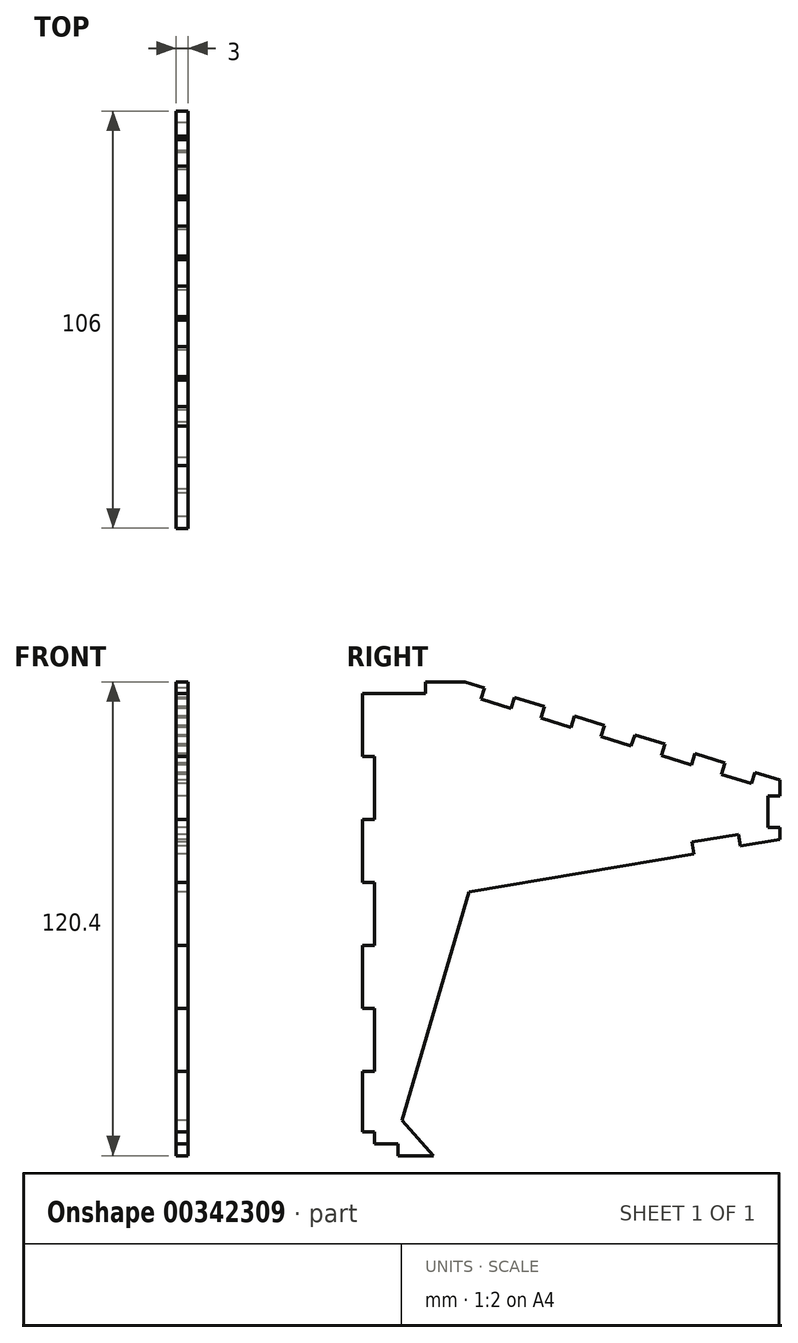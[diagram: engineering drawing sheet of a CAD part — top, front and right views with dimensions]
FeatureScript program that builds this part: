
annotation { "Feature Type Name" : "Feature", "Feature Type Description" : "" }
export const myFeature = defineFeature(function(context is Context, id is Id, definition is map)
    precondition{}
    {
        {
            var Q0;
            Q0=qCreatedBy(makeId("Right.planeOp"),FACE);
            var sketch = newSketch(context, id + "F0", { "sketchPlane" : qUnion([Q0])});
            skLineSegment(sketch, "E0.top", {"start": v(-28.67, -48.45) * mm, "end": v(-19.67, -48.45) * mm});
            skLineSegment(sketch, "E1", {"start": v(-37.67, 71.95) * mm, "end": v(-21.67, 71.95) * mm, "construction": true});
            skLineSegment(sketch, "E2", {"start": v(-21.67, 71.95) * mm, "end": v(-11.67, 71.95) * mm});
            skLineSegment(sketch, "E3", {"start": v(-21.67, 71.95) * mm, "end": v(-21.67, 68.95) * mm});
            skLineSegment(sketch, "E4", {"start": v(-21.67, 68.95) * mm, "end": v(-37.67, 68.95) * mm});
            skLineSegment(sketch, "E5", {"start": v(-37.67, 68.95) * mm, "end": v(-37.67, 52.95) * mm});
            skLineSegment(sketch, "E6", {"start": v(-37.67, 52.95) * mm, "end": v(-34.67, 52.95) * mm});
            skLineSegment(sketch, "E7", {"start": v(-34.67, 52.95) * mm, "end": v(-34.67, 36.95) * mm});
            skLineSegment(sketch, "E8", {"start": v(-34.67, 36.95) * mm, "end": v(-37.67, 36.95) * mm});
            skLineSegment(sketch, "E9", {"start": v(-37.67, 36.95) * mm, "end": v(-37.67, 20.95) * mm});
            skLineSegment(sketch, "E10", {"start": v(-37.67, 20.95) * mm, "end": v(-34.67, 20.95) * mm});
            skLineSegment(sketch, "E11", {"start": v(-34.67, 20.95) * mm, "end": v(-34.67, 4.95) * mm});
            skLineSegment(sketch, "E12", {"start": v(-34.67, 4.95) * mm, "end": v(-37.67, 4.95) * mm});
            skLineSegment(sketch, "E13", {"start": v(-37.67, 4.95) * mm, "end": v(-37.67, -11.05) * mm});
            skLineSegment(sketch, "E14", {"start": v(-37.67, -11.05) * mm, "end": v(-34.67, -11.05) * mm});
            skLineSegment(sketch, "E15", {"start": v(-34.67, -11.05) * mm, "end": v(-34.67, -27.05) * mm});
            skLineSegment(sketch, "E16", {"start": v(-34.67, -27.05) * mm, "end": v(-37.67, -27.05) * mm});
            skLineSegment(sketch, "E17", {"start": v(-37.67, -27.05) * mm, "end": v(-37.67, -42.45) * mm});
            skLineSegment(sketch, "E18", {"start": v(-37.67, -42.45) * mm, "end": v(-34.67, -42.45) * mm});
            skLineSegment(sketch, "E19", {"start": v(-34.67, -42.45) * mm, "end": v(-34.67, -45.45) * mm});
            skLineSegment(sketch, "E20", {"start": v(-34.67, -45.45) * mm, "end": v(-28.67, -45.45) * mm});
            skLineSegment(sketch, "E21", {"start": v(-28.67, -45.45) * mm, "end": v(-28.67, -48.45) * mm});
            skLineSegment(sketch, "E22", {"start": v(68.33, 46.95) * mm, "end": v(68.33, 42.95) * mm});
            skLineSegment(sketch, "E23", {"start": v(68.33, 42.95) * mm, "end": v(65.33, 42.95) * mm});
            skLineSegment(sketch, "E24", {"start": v(65.33, 42.95) * mm, "end": v(65.33, 34.95) * mm});
            skLineSegment(sketch, "E25", {"start": v(65.33, 34.95) * mm, "end": v(68.33, 34.95) * mm});
            skLineSegment(sketch, "E26", {"start": v(68.33, 34.95) * mm, "end": v(68.33, 31.95) * mm});
            skLineSegment(sketch, "E27", {"start": v(-19.67, -48.45) * mm, "end": v(-27.67, -39.45) * mm});
            skLineSegment(sketch, "E28", {"start": v(-10.67, 18.55) * mm, "end": v(-27.67, -39.45) * mm});
            skLineSegment(sketch, "E29", {"start": v(46.5, 28.24) * mm, "end": v(46, 31.2) * mm});
            skLineSegment(sketch, "E30", {"start": v(46, 31.2) * mm, "end": v(57.83, 33.2) * mm});
            skLineSegment(sketch, "E31", {"start": v(57.83, 33.2) * mm, "end": v(58.33, 30.25) * mm});
            skLineSegment(sketch, "E32", {"start": v(-10.67, 18.55) * mm, "end": v(46.5, 28.24) * mm});
            skLineSegment(sketch, "E33", {"start": v(58.33, 30.25) * mm, "end": v(68.33, 31.95) * mm});
            skLineSegment(sketch, "E34", {"start": v(46.5, 28.24) * mm, "end": v(58.33, 30.25) * mm, "construction": true});
            skLineSegment(sketch, "E35", {"start": v(68.33, 46.95) * mm, "end": v(68.33, 56.95) * mm, "construction": true});
            skLineSegment(sketch, "E36", {"start": v(-11.67, 81.95) * mm, "end": v(-11.67, 71.95) * mm, "construction": true});
            skLineSegment(sketch, "E37", {"start": v(61.98, 48.93) * mm, "end": v(61.09, 46.07) * mm});
            skLineSegment(sketch, "E38", {"start": v(61.09, 46.07) * mm, "end": v(53.45, 48.45) * mm});
            skLineSegment(sketch, "E39", {"start": v(53.45, 48.45) * mm, "end": v(54.35, 51.32) * mm});
            skLineSegment(sketch, "E40", {"start": v(54.35, 51.32) * mm, "end": v(46.7, 53.7) * mm});
            skLineSegment(sketch, "E41", {"start": v(46.7, 53.7) * mm, "end": v(45.82, 50.84) * mm});
            skLineSegment(sketch, "E42", {"start": v(45.82, 50.84) * mm, "end": v(38.18, 53.22) * mm});
            skLineSegment(sketch, "E43", {"start": v(38.18, 53.22) * mm, "end": v(39.07, 56.09) * mm});
            skLineSegment(sketch, "E44", {"start": v(39.07, 56.09) * mm, "end": v(31.44, 58.47) * mm});
            skLineSegment(sketch, "E45", {"start": v(31.44, 58.47) * mm, "end": v(30.54, 55.61) * mm});
            skLineSegment(sketch, "E46", {"start": v(30.54, 55.61) * mm, "end": v(22.9, 58) * mm});
            skLineSegment(sketch, "E47", {"start": v(22.9, 58) * mm, "end": v(23.8, 60.86) * mm});
            skLineSegment(sketch, "E48", {"start": v(23.8, 60.86) * mm, "end": v(16.17, 63.25) * mm});
            skLineSegment(sketch, "E49", {"start": v(16.17, 63.25) * mm, "end": v(15.27, 60.38) * mm});
            skLineSegment(sketch, "E50", {"start": v(15.27, 60.38) * mm, "end": v(7.64, 62.77) * mm});
            skLineSegment(sketch, "E51", {"start": v(7.64, 62.77) * mm, "end": v(8.53, 65.63) * mm});
            skLineSegment(sketch, "E52", {"start": v(8.53, 65.63) * mm, "end": v(0.9, 68.02) * mm});
            skLineSegment(sketch, "E53", {"start": v(0.9, 68.02) * mm, "end": v(0, 65.16) * mm});
            skLineSegment(sketch, "E54", {"start": v(0, 65.16) * mm, "end": v(-7.64, 67.54) * mm});
            skLineSegment(sketch, "E55", {"start": v(-7.64, 67.54) * mm, "end": v(-6.74, 70.4) * mm});
            skLineSegment(sketch, "E56", {"start": v(-11.67, 71.95) * mm, "end": v(-6.74, 70.4) * mm});
            skLineSegment(sketch, "E57", {"start": v(68.33, 46.95) * mm, "end": v(61.98, 48.93) * mm});
            skSolve(sketch);
        }
        {
            var Q0;
            Q0 = qSketchRegion(id + "F0", true);
            extrude(context, id + "F1", {"entities" : qUnion([Q0]), "offsetDistance" : 25 * mm, "depth" : 3 * mm});
        }
    });
